# Revit family: Rohrschellen Form A, Typ TGA, fvz
name_source: partatom
category: HLS-Bauteile
revit_build: Autodesk Revit 2017 (Build: 20190507_1515(x64)
units: mm (PartAtom-declared; Revit-internal decimal feet)

## family parameters
Arbeitsebenenbasiert = Ja
Beim Laden mit Abzugskörper schneiden = Nein
Bemaßung runder Anschluss = Durchmesser verwenden
Gemeinsam genutzt = Ja
Immer vertikal = Nein
Raumberechnungspunkt = Nein
Teiletyp = Normal

## types (17) — shared parameters
Anschluss = ohne Anschluss
Bauart = zweiteilig
Fabrikat = MEFA
Firma = MEFA Befestigungs- und Montagesysteme GmbH
Material = Stahl
Mengeneinheit = St
Oberflaeche = feuerstückverzinkt
Rohraußendurchmesser Zoll = Zoll
Vorgabe-Ansicht = 1219 mm
max. zul. Last horizontal = 0.00 kN
max. zul. Last vertikal = 0.00 kN
vpe = 1 St
zero-valued in all types: AB, DS, HGA, Nennweite DN Rohr, Stärke Material, max. Rohraußendurchmesser, min. Rohraußendurchmesser

## per-type parameters (varying)
| type | A | Achsabstand | Artikelnummer | B | C | D | DF1 | DF2 | DVS | EAN | Gewicht | Gewicht pro Bauteil | H | Kurztext1 | Kurztext2 | MB | MD | Materialmaße | RM | Rohraußendurchmesser | S | Verschluss-Schraube |
| Rohrschellen Form A, Typ TGA, Ø 219, fvz | 6 mm  [stored 0.019685 ft] | 288 mm | 109ffaa0219 | 336 mm | 24 mm  [stored 0.0787402 ft] | 219 mm  [stored 0.718504 ft] | 48 mm  [stored 0.15748 ft] | 40 mm  [stored 0.131234 ft] | 17 mm | 4250928423467 | 2.54 kg | 2.54 kg | 231 mm  [stored 0.757874 ft] | Rohrschelle Form A TGA 60x6,0 | 219 mm ohne Anschluss fsv | 60 mm  [stored 0.19685 ft] | 6 mm  [stored 0.019685 ft] | 60x6,0 mm | 116 mm | 219 mm  [stored 0.718504 ft] | 288 mm  [stored 0.944882 ft] | M16 |
| Rohrschellen Form A, Typ TGA, Ø 267, fvz | 6 mm  [stored 0.019685 ft] | 337 mm | 109ffaa0267 | 385 mm | 24 mm  [stored 0.0787402 ft] | 267 mm  [stored 0.875984 ft] | 48 mm  [stored 0.15748 ft] | 41 mm  [stored 0.134514 ft] | 17 mm | 4250928423474 | 3.00 kg | 3.00 kg | 279 mm | Rohrschelle Form A TGA 60x6,0 | 267 mm ohne Anschluss fsv | 60 mm  [stored 0.19685 ft] | 6 mm  [stored 0.019685 ft] | 60x6,0 mm | 140 mm | 267 mm  [stored 0.875984 ft] | 337 mm | M16 |
| Rohrschellen Form A, Typ TGA, Ø 273, fvz | 6 mm  [stored 0.019685 ft] | 343 mm | 109ffaa0273 | 391 mm | 24 mm  [stored 0.0787402 ft] | 273 mm  [stored 0.895669 ft] | 48 mm  [stored 0.15748 ft] | 41 mm  [stored 0.134514 ft] | 17 mm | 4250928423481 | 3.05 kg | 3.05 kg | 285 mm  [stored 0.935039 ft] | Rohrschelle Form A TGA 60x6,0 | 273 mm ohne Anschluss fsv | 60 mm  [stored 0.19685 ft] | 6 mm  [stored 0.019685 ft] | 60x6,0 mm | 143 mm | 273 mm  [stored 0.895669 ft] | 343 mm | M16 |
| Rohrschellen Form A, Typ TGA, Ø 324, fvz | 6 mm  [stored 0.019685 ft] | 343 mm | 109ffaa0273 | 443 mm | 24 mm  [stored 0.0787402 ft] | 324 mm | 48 mm  [stored 0.15748 ft] | 42 mm  [stored 0.137795 ft] | 17 mm | 4250928423481 | 3.05 kg | 3.05 kg | 336 mm | Rohrschelle Form A TGA 60x6,0 | 273 mm ohne Anschluss fsv | 60 mm  [stored 0.19685 ft] | 6 mm  [stored 0.019685 ft] | 60x6,0 mm | 168 mm | 273 mm  [stored 0.895669 ft] | 395 mm | M16 |
| Rohrschellen Form A, Typ TGA, Ø 356, fvz | 8 mm  [stored 0.0262467 ft] | 430 mm | 109fgaa0356 | 478 mm | 24 mm  [stored 0.0787402 ft] | 356 mm | 48 mm  [stored 0.15748 ft] | 41 mm  [stored 0.134514 ft] | 17 mm | 4250928423504 | 5.06 kg | 5.06 kg | 372 mm | Rohrschelle Form A TGA 60x8,0 | 356 mm ohne Anschluss fsv | 60 mm  [stored 0.19685 ft] | 8 mm  [stored 0.0262467 ft] | 60x8,0 mm | 186 mm  [stored 0.610236 ft] | 356 mm | 430 mm | M16 |
| Rohrschellen Form A, Typ TGA, Ø 368, fvz | 8 mm  [stored 0.0262467 ft] | 442 mm | 109fgaa0368 | 490 mm | 24 mm  [stored 0.0787402 ft] | 368 mm | 48 mm  [stored 0.15748 ft] | 41 mm  [stored 0.134514 ft] | 17 mm | 4250928423511 | 5.21 kg | 5.21 kg | 384 mm | Rohrschelle Form A TGA 60x8,0 | 368 mm ohne Anschluss fsv | 60 mm  [stored 0.19685 ft] | 8 mm  [stored 0.0262467 ft] | 60x8,0 mm | 192 mm  [stored 0.629921 ft] | 368 mm | 442 mm | M16 |
| Rohrschellen Form A, Typ TGA, Ø 406, fvz | 8 mm  [stored 0.0262467 ft] | 481 mm | 109fgaa0406 | 529 mm | 24 mm  [stored 0.0787402 ft] | 406 mm | 48 mm  [stored 0.15748 ft] | 42 mm  [stored 0.137795 ft] | 17 mm | 4250928423528 | 5.68 kg | 5.68 kg | 422 mm | Rohrschelle Form A TGA 60x8,0 | 406 mm ohne Anschluss fsv | 60 mm  [stored 0.19685 ft] | 8 mm  [stored 0.0262467 ft] | 60x8,0 mm | 211 mm  [stored 0.692257 ft] | 406 mm | 481 mm | M16 |
| Rohrschellen Form A, Typ TGA, Ø 419, fvz | 8 mm  [stored 0.0262467 ft] | 494 mm | 109fgaa0419 | 542 mm | 24 mm  [stored 0.0787402 ft] | 419 mm | 48 mm  [stored 0.15748 ft] | 42 mm  [stored 0.137795 ft] | 17 mm | 4250928423535 | 5.85 kg | 5.85 kg | 435 mm | Rohrschelle Form A TGA 60x8,0 | 419 mm ohne Anschluss fsv | 60 mm  [stored 0.19685 ft] | 8 mm  [stored 0.0262467 ft] | 60x8,0 mm | 218 mm | 419 mm | 494 mm | M16 |
| Rohrschellen Form A, Typ TGA, Ø 457, fvz | 8 mm  [stored 0.0262467 ft] | 532 mm | 109fgaa0457 | 580 mm | 24 mm  [stored 0.0787402 ft] | 457 mm | 48 mm  [stored 0.15748 ft] | 42 mm  [stored 0.137795 ft] | 17 mm | 4250928423542 | 6.31 kg | 6.31 kg | 473 mm | Rohrschelle Form A TGA 60x8,0 | 457 mm ohne Anschluss fsv | 60 mm  [stored 0.19685 ft] | 8 mm  [stored 0.0262467 ft] | 60x8,0 mm | 237 mm | 457 mm | 532 mm | M16 |
| Rohrschellen Form A, Typ TGA, Ø 508, fvz | 10 mm  [stored 0.0328084 ft] | 598 mm | 109fhaa0508 | 658 mm | 30 mm  [stored 0.0984252 ft] | 508 mm | 60 mm  [stored 0.19685 ft] | 47 mm  [stored 0.154199 ft] | 23 mm  [stored 0.0754593 ft] | 4250928423559 | 10.23 kg | 10.23 kg | 528 mm | Rohrschelle Form A TGA 70x10,0 | 508 mm ohne Anschluss fsv | 70 mm  [stored 0.229659 ft] | 10 mm  [stored 0.0328084 ft] | 70x10,0 mm | 264 mm  [stored 0.866142 ft] | 508 mm | 598 mm | M20 |
| Rohrschellen Form A, Typ TGA, Ø 521, fvz | 10 mm  [stored 0.0328084 ft] | 611 mm | 109fhaa0521 | 671 mm | 30 mm  [stored 0.0984252 ft] | 521 mm | 60 mm  [stored 0.19685 ft] | 47 mm  [stored 0.154199 ft] | 23 mm  [stored 0.0754593 ft] | 4250928423566 | 10.46 kg | 10.46 kg | 541 mm | Rohrschelle Form A TGA 70x10,0 | 521 mm ohne Anschluss fsv | 70 mm  [stored 0.229659 ft] | 10 mm  [stored 0.0328084 ft] | 70x10,0 mm | 271 mm | 521 mm | 611 mm | M20 |
| Rohrschellen Form A, Typ TGA, Ø 610, fvz | 10 mm  [stored 0.0328084 ft] | 700 mm | 109fhaa0610 | 760 mm | 30 mm  [stored 0.0984252 ft] | 610 mm | 60 mm  [stored 0.19685 ft] | 47 mm  [stored 0.154199 ft] | 23 mm  [stored 0.0754593 ft] | 4250928423573 | 12.07 kg | 12.07 kg | 630 mm | Rohrschelle Form A TGA 70x10,0 | 610 mm ohne Anschluss fsv | 70 mm  [stored 0.229659 ft] | 10 mm  [stored 0.0328084 ft] | 70x10,0 mm | 315 mm | 610 mm | 700 mm | M20 |
| Rohrschellen Form A, Typ TGA, Ø 711, fvz | 10 mm  [stored 0.0328084 ft] | 802 mm | 109fhaa0711 | 862 mm | 30 mm  [stored 0.0984252 ft] | 711 mm | 60 mm  [stored 0.19685 ft] | 48 mm  [stored 0.15748 ft] | 23 mm  [stored 0.0754593 ft] | 4250928423580 | 13.88 kg | 13.88 kg | 731 mm | Rohrschelle Form A TGA 70x10,0 | 711 mm ohne Anschluss fsv | 70 mm  [stored 0.229659 ft] | 10 mm  [stored 0.0328084 ft] | 70x10,0 mm | 366 mm | 711 mm | 802 mm | M20 |
| Rohrschellen Form A, Typ TGA, Ø 813, fvz | 10 mm  [stored 0.0328084 ft] | 904 mm | 109fhaa0813 | 964 mm | 30 mm  [stored 0.0984252 ft] | 813 mm | 60 mm  [stored 0.19685 ft] | 48 mm  [stored 0.15748 ft] | 23 mm  [stored 0.0754593 ft] | 4250928423597 | 15.72 kg | 15.72 kg | 833 mm | Rohrschelle Form A TGA 70x10,0 | 813 mm ohne Anschluss fsv | 70 mm  [stored 0.229659 ft] | 10 mm  [stored 0.0328084 ft] | 70x10,0 mm | 417 mm | 813 mm | 904 mm | M20 |
| Rohrschellen Form A, Typ TGA, Ø 914, fvz | 15 mm  [stored 0.0492126 ft] | 1034 mm | 109fkaa0914 | 1106 mm | 36 mm  [stored 0.11811 ft] | 914 mm | 72 mm  [stored 0.23622 ft] | 63 mm  [stored 0.206693 ft] | 27 mm  [stored 0.0885827 ft] | 4250928423603 | 33.42 kg | 33.42 kg | 944 mm | Rohrschelle Form A TGA 90x15,0 | 914 mm ohne Anschluss fsv | 90 mm  [stored 0.295276 ft] | 15 mm  [stored 0.0492126 ft] | 90x15,0 mm | 472 mm | 914 mm | 1034 mm | M24 |
| Rohrschellen Form A, Typ TGA, Ø1016, fvz | 15 mm  [stored 0.0492126 ft] | 1137 mm | 109fkaa1016 | 1209 mm | 36 mm  [stored 0.11811 ft] | 1016 mm | 72 mm  [stored 0.23622 ft] | 64 mm  [stored 0.209974 ft] | 27 mm  [stored 0.0885827 ft] | 4250928423610 | 37.82 kg | 37.82 kg | 1046 mm | Rohrschelle Form A TGA 90x15,0 | 1016 mm ohne Anschluss fsv | 90 mm  [stored 0.295276 ft] | 15 mm  [stored 0.0492126 ft] | 90x15,0 mm | 523 mm | 1016 mm | 1137 mm | M24 |
| Rohrschellen Form A, Typ TGA, Ø1220, fvz | 15 mm  [stored 0.0492126 ft] | 1341 mm | 109fkaa1220 | 1413 mm | 36 mm  [stored 0.11811 ft] | 1220 mm | 72 mm  [stored 0.23622 ft] | 64 mm  [stored 0.209974 ft] | 27 mm  [stored 0.0885827 ft] | 4250928423627 | 45.06 kg | 45.06 kg | 1250 mm | Rohrschelle Form A TGA 90x15,0 | 1220 mm ohne Anschluss fsv | 90 mm  [stored 0.295276 ft] | 15 mm  [stored 0.0492126 ft] | 90x15,0 mm | 625 mm | 1220 mm | 1341 mm | M24 |

note: [stored X ft] marks values corroborated as IEEE doubles in the binary element streams (Revit-internal decimal feet)
